# Revit family: Шкафы климатические навесные (с крышей)
name_source: partatom
category: Обобщенные модели
units: mm (PartAtom-declared; Revit-internal decimal feet)

## family parameters
Всегда вертикально = Да
Может служить основой для арматурных стержней = Нет
На основе рабочей плоскости = Нет
Общий = Нет
При загрузке вырезать с полостями = Нет
Размер круглого соединителя = Использовать диаметр
Тип детали = Нормальный
Точка расчета площади = Нет

## types (9) — shared parameters
ADSK_URL документации изделия = sert_shkt.PDF (ssd.ru)
ADSK_Единица измерения = шт
ADSK_Завод-изготовитель = АО СВЯЗЬСТРОЙДЕТАЛЬ
ADSK_Размер_Ширина = 700 мм
Материал Каркаса = RAL 7035
Материал букв = Металл красный
Материал крепежей = Металл черный
Толщина -4 = -4 мм
Толщина 2 = 2 мм
Толщина 25 = 25 мм
Толщина 4 = 4 мм
Толщина 5 = 5 мм
zero-valued in all types: Ноль

## per-type parameters (varying)
| type | ADSK_URL страницы изделия | ADSK_Код изделия | ADSK_Наименование | ADSK_Наименование краткое | ADSK_Размер_Высота | ADSK_Размер_Глубина | Описание |
| ШКТ-НВ-2-12U (700х500 мм) | Шкаф климатический телекоммуникационный навесной ШКТ-НВ-2-12U-600-500 с крышей ССД ( 130411-00890 ) (ssd.ru) | 130411-00890 | Шкаф климатический телекоммуникационный навесной ШКТ-НВ-2-12U-600-500 с крышей ССД | ШКТ-НВ-2-12U (700х500мм) | 677 мм | 559 мм | Шкаф климатический телекоммуникационный навесной ШКТ-НВ-2-12U-600-500 с крышей ССД |
| ШКТ-НВ-2-12U (700х600 мм) | Шкаф климатический телекоммуникационный навесной ШКТ-НВ-2-12U-600-600 с крышей ССД ( 130411-00891 ) (ssd.ru) | 130411-00891 | Шкаф климатический телекоммуникационный навесной ШКТ-НВ-2-12U-600-600 с крышей ССД | ШКТ-НВ-2-12U (700х600мм) | 677 мм | 659 мм | Шкаф климатический телекоммуникационный навесной ШКТ-НВ-2-12U-600-600 с крышей ССД |
| ШКТ-НВ-2-12U (700х800 мм) | Шкаф климатический телекоммуникационный навесной ШКТ-НВ-2-12U-600-800 с крышей ССД ( 130411-00896 ) (ssd.ru) | 130411-00896 | Шкаф климатический телекоммуникационный навесной ШКТ-НВ-2-12U-600-800 с крышей ССД | ШКТ-НВ-2-12U (700х800мм) | 677 мм | 859 мм | Шкаф климатический телекоммуникационный навесной ШКТ-НВ-2-12U-600-800 с крышей ССД |
| ШКТ-НВ-2-15U (700х500мм) | Шкаф климатический телекоммуникационный навесной ШКТ-НВ-2-15U-600-500 с крышей ССД ( 130411-00892 ) (ssd.ru) | 130411-00892 | Шкаф климатический телекоммуникационный навесной ШКТ-НВ-2-15U-600-500 с крышей ССД | ШКТ-НВ-2-15U (700х500мм) | 810 мм | 559 мм | Шкаф климатический телекоммуникационный навесной ШКТ-НВ-2-15U-600-500 с крышей ССД |
| ШКТ-НВ-2-15U (700х600мм) | Шкаф климатический телекоммуникационный навесной ШКТ-НВ-2-15U-600-600 с крышей ССД ( 130411-00893 ) (ssd.ru) | 130411-00893 | Шкаф климатический телекоммуникационный навесной ШКТ-НВ-2-15U-600-600 с крышей ССД | ШКТ-НВ-2-15U (700х600мм) | 810 мм | 659 мм | Шкаф климатический телекоммуникационный навесной ШКТ-НВ-2-15U-600-600 с крышей ССД |
| ШКТ-НВ-2-15U (700х800мм) | Шкаф климатический телекоммуникационный навесной ШКТ-НВ-2-15U-600-800 с крышей ССД ( 130411-00898 ) (ssd.ru) | 130411-00898 | Шкаф климатический телекоммуникационный навесной ШКТ-НВ-2-15U-600-800 с крышей ССД | ШКТ-НВ-2-15U (700х800мм) | 810 мм | 859 мм | Шкаф климатический телекоммуникационный навесной ШКТ-НВ-2-15U-600-800 с крышей ССД |
| ШКТ-НВ-2-18U (700х500мм) | Шкаф климатический телекоммуникационный навесной ШКТ-НВ-2-18U-600-500 с крышей ССД ( 130411-00894 ) (ssd.ru) | 130411-00894 | Шкаф климатический телекоммуникационный навесной ШКТ-НВ-2-18U-600-500 с крышей ССД | ШКТ-НВ-2-18U (700х500мм) | 943 мм | 559 мм | Шкаф климатический телекоммуникационный навесной ШКТ-НВ-2-18U-600-500 с крышей ССД |
| ШКТ-НВ-2-18U (700х600мм) | Шкаф климатический телекоммуникационный навесной ШКТ-НВ-2-18U-600-600 с крышей ССД ( 130411-00895 ) (ssd.ru) | 130411-00895 | Шкаф климатический телекоммуникационный навесной ШКТ-НВ-2-18U-600-600 с крышей ССД | ШКТ-НВ-2-18U (700х600мм) | 943 мм | 659 мм | Шкаф климатический телекоммуникационный навесной ШКТ-НВ-2-18U-600-600 с крышей ССД |
| ШКТ-НВ-2-18U (700х800мм) | Шкаф климатический телекоммуникационный навесной ШКТ-НВ-2-18U-600-800 с крышей ССД ( 130411-00897 ) (ssd.ru) | 130411-00897 | Шкаф климатический телекоммуникационный навесной ШКТ-НВ-2-18U-600-800 с крышей ССД | ШКТ-НВ-2-18U (700х800мм) | 943 мм | 853 мм | Шкаф климатический телекоммуникационный навесной ШКТ-НВ-2-18U-600-800 с крышей ССД |

## geometry (parser evidence)
native form markers: Blend x2
no freeform markers — native parametric forms only
